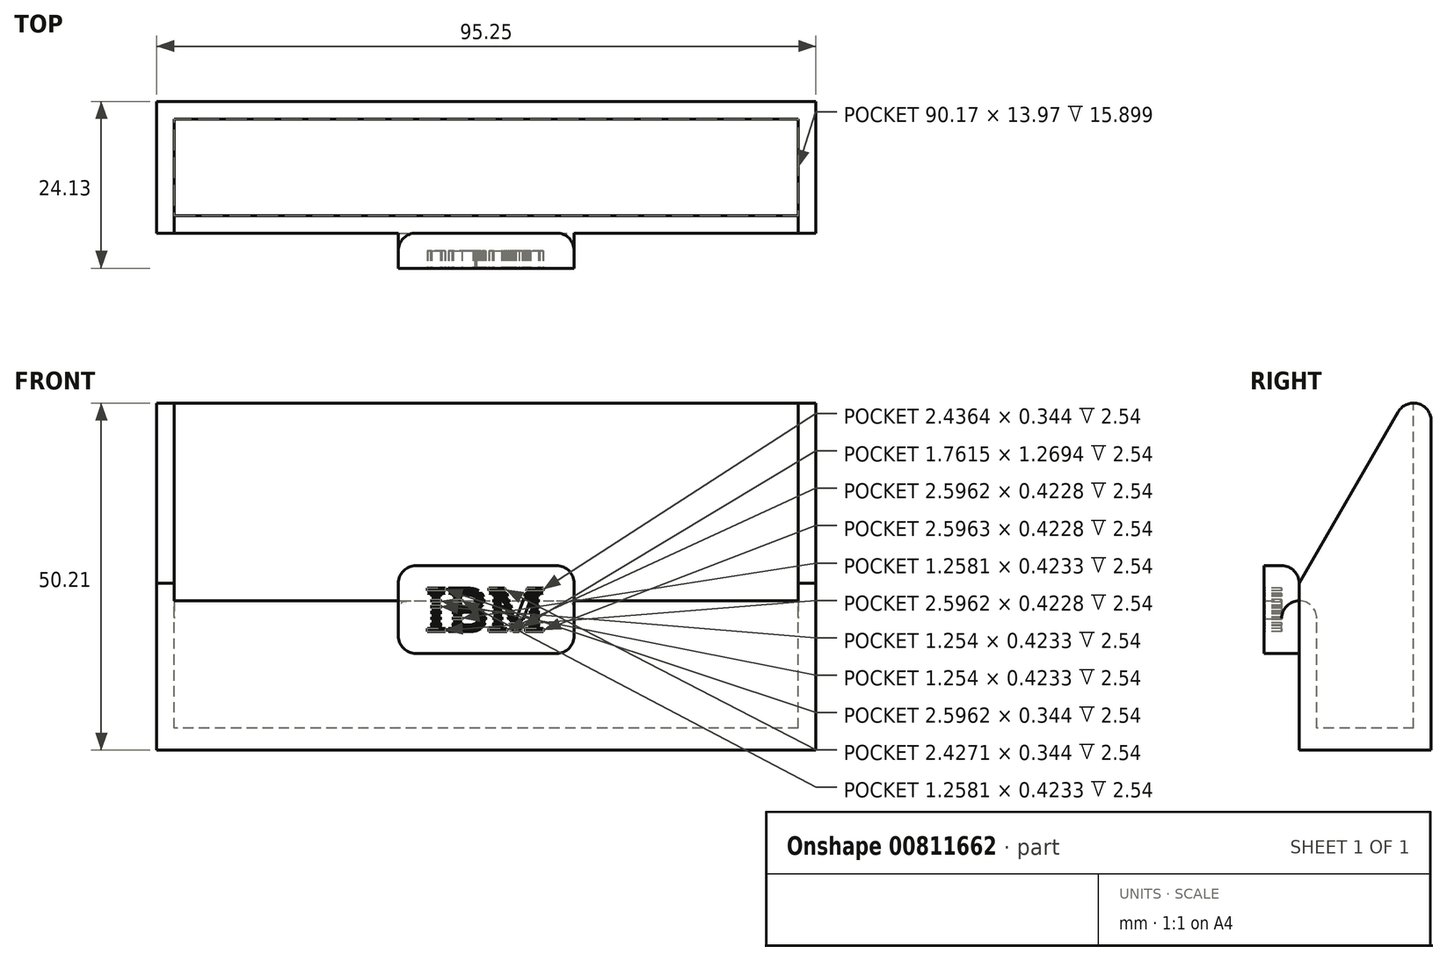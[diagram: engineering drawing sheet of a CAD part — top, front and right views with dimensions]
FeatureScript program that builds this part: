
annotation { "Feature Type Name" : "Feature", "Feature Type Description" : "" }
export const myFeature = defineFeature(function(context is Context, id is Id, definition is map)
    precondition{}
    {
        {
            var Q0;
            Q0=qCreatedBy(makeId("Top.planeOp"),FACE);
            var sketch = newSketch(context, id + "F0", { "sketchPlane" : qUnion([Q0])});
            skLineSegment(sketch, "E0.bottom", {"start": v(0, 0) * mm, "end": v(95.25, 0) * mm});
            skLineSegment(sketch, "E0.top", {"start": v(0, 19.05) * mm, "end": v(95.25, 19.05) * mm});
            skLineSegment(sketch, "E0.left", {"start": v(0, 0) * mm, "end": v(0, 19.05) * mm});
            skLineSegment(sketch, "E0.right", {"start": v(95.25, 0) * mm, "end": v(95.25, 19.05) * mm});
            skSolve(sketch);
        }
        {
            var Q0;
            Q0=makeQuery(id+"F0.imprint","IMPRINT",FACE,{"disambiguationData":[TD([[makeQuery(id+"F0.imprint","IMPRINT",EDGE,{"derivedFrom":sQuery(id+"F0.wireOp",EDGE,"E0.bottom")}),1.0]])]});
            extrude(context, id + "F1", {"entities" : qUnion([Q0]), "depth" : 57.15 * mm, "offsetDistance" : 25.4 * mm});
        }
        {
            var Q0;
            Q0=makeQuery(id+"F1.opExtrude","CAP_FACE",FACE,{"disambiguationData":[OSD([sQuery(id+"F0.wireOp",EDGE,"E0.bottom"),sQuery(id+"F0.wireOp",EDGE,"E0.top"),sQuery(id+"F0.wireOp",EDGE,"E0.left"),sQuery(id+"F0.wireOp",EDGE,"E0.right")])],"isStart":false});
            var sketch = newSketch(context, id + "F2", { "sketchPlane" : qUnion([Q0])});
            skLineSegment(sketch, "E1.bottom", {"start": v(92.71, 16.5) * mm, "end": v(2.54, 16.5) * mm});
            skLineSegment(sketch, "E1.top", {"start": v(92.71, 2.54) * mm, "end": v(2.54, 2.54) * mm});
            skLineSegment(sketch, "E1.left", {"start": v(92.71, 16.5) * mm, "end": v(92.71, 2.54) * mm});
            skLineSegment(sketch, "E1.right", {"start": v(2.54, 16.5) * mm, "end": v(2.54, 2.54) * mm});
            skPoint(sketch, "E1.middle", {"position": v(47.63, 9.52) * mm});
            skPoint(sketch, "E1.middle.positionSnap0", {"position": v(0, 9.52) * mm});
            skPoint(sketch, "E1.middle.positionSnap1", {"position": v(47.63, 19.05) * mm});
            skPoint(sketch, "E1.centerSnap0", {"position": v(0, 9.52) * mm});
            skPoint(sketch, "E1.centerSnap1", {"position": v(47.63, 19.05) * mm});
            skSolve(sketch);
        }
        {
            var Q0;
            Q0=makeQuery(id+"F2.imprint","IMPRINT",FACE,{"disambiguationData":[TD([[makeQuery(id+"F2.imprint","IMPRINT",EDGE,{"derivedFrom":sQuery(id+"F2.wireOp",EDGE,"E1.bottom")}),1.0]])]});
            extrude(context, id + "F3", {"entities" : qUnion([Q0]), "operationType" : NewBodyOperationType.REMOVE, "oppositeDirection" : true, "depth" : 53.97 * mm, "offsetDistance" : 25.4 * mm});
        }
        {
            var Q0;
            Q0=makeQuery(id+"F1.opExtrude","CAP_FACE",FACE,{"disambiguationData":[OSD([sQuery(id+"F0.wireOp",EDGE,"E0.bottom"),sQuery(id+"F0.wireOp",EDGE,"E0.top"),sQuery(id+"F0.wireOp",EDGE,"E0.left"),sQuery(id+"F0.wireOp",EDGE,"E0.right")])],"isStart":false});
            var Q1;
            Q1=makeQuery(id+"F1.opExtrude","CAP_EDGE",EDGE,{"disambiguationData":[OSD([sQuery(id+"F0.wireOp",EDGE,"E0.top")])],"isStart":false});
            cPlane(context, id + "F4", {"entities" : qUnion([Q0, Q1]), "cplaneType" : CPlaneType.LINE_ANGLE, "offset" : 25.4 * mm, "angle" : 60 * degree, "width" : 152.4 * mm, "height" : 152.4 * mm});
        }
        {
            var Q0;
            Q0=qCreatedBy(id+"F4.planeOp",FACE);
            var sketch = newSketch(context, id + "F5", { "sketchPlane" : qUnion([Q0])});
            skLineSegment(sketch, "E2.bottom", {"start": v(0, 59.02) * mm, "end": v(-95.25, 59.02) * mm});
            skLineSegment(sketch, "E2.top", {"start": v(0, 19.65) * mm, "end": v(-95.25, 19.65) * mm});
            skLineSegment(sketch, "E2.left", {"start": v(0, 59.02) * mm, "end": v(0, 19.65) * mm});
            skLineSegment(sketch, "E2.right", {"start": v(-95.25, 59.02) * mm, "end": v(-95.25, 19.65) * mm});
            skSolve(sketch);
        }
        {
            var Q0;
            Q0 = qSketchRegion(id + "F5", true);
            extrude(context, id + "F6", {"entities" : qUnion([Q0]), "operationType" : NewBodyOperationType.REMOVE, "oppositeDirection" : true, "depth" : 25.4 * mm, "offsetDistance" : 25.4 * mm});
        }
        {
            var Q0;
            Q0=makeQuery(id+"F6.boolean.opBoolean","MERGE",EDGE,{"derivedFrom":[makeQuery(id+"F1.opExtrude","CAP_EDGE",EDGE,{"disambiguationData":[OSD([sQuery(id+"F0.wireOp",EDGE,"E0.top")])],"isStart":false}),makeQuery(id+"F6.opExtrude","CAP_EDGE",EDGE,{"disambiguationData":[OSD([sQuery(id+"F5.wireOp",EDGE,"E2.bottom")])],"isStart":true})]});
            var Q1;
            Q1=makeQuery(id+"F6.boolean.opBoolean","INTERSECT",EDGE,{"derivedFrom":[makeQuery(id+"F3.boolean.opBoolean","COPY",FACE,{"derivedFrom":makeQuery(id+"F3.opExtrude","SWEPT_FACE",FACE,{"disambiguationData":[OSD([sQuery(id+"F2.wireOp",EDGE,"E1.top")])]})}),makeQuery(id+"F6.opExtrude","CAP_FACE",FACE,{"disambiguationData":[OSD([sQuery(id+"F5.wireOp",EDGE,"E2.bottom"),sQuery(id+"F5.wireOp",EDGE,"E2.top"),sQuery(id+"F5.wireOp",EDGE,"E2.left"),sQuery(id+"F5.wireOp",EDGE,"E2.right")])],"isStart":true})]});
            fillet(context, id + "F7", {"entities" : qUnion([Q0, Q1]), "radius" : 2.54 * mm, "tangentPropagation" : true, "allowEdgeOverflow" : false});
        }
        {
            var Q0;
            Q0=makeQuery(id+"F1.opExtrude","SWEPT_FACE",FACE,{"disambiguationData":[OSD([sQuery(id+"F0.wireOp",EDGE,"E0.bottom")])]});
            var sketch = newSketch(context, id + "F8", { "sketchPlane" : qUnion([Q0])});
            skLineSegment(sketch, "E3.bottom", {"start": v(57.79, 26.7) * mm, "end": v(37.47, 26.7) * mm});
            skLineSegment(sketch, "E3.top", {"start": v(57.79, 14) * mm, "end": v(37.47, 14) * mm});
            skLineSegment(sketch, "E3.left", {"start": v(60.33, 24.15) * mm, "end": v(60.33, 16.53) * mm});
            skLineSegment(sketch, "E3.right", {"start": v(34.93, 24.15) * mm, "end": v(34.93, 16.53) * mm});
            skPoint(sketch, "E3.middle", {"position": v(47.63, 20.34) * mm});
            skPoint(sketch, "E3.middle.positionSnap0", {"position": v(47.63, 21.61) * mm});
            skPoint(sketch, "E3.centerSnap0", {"position": v(47.63, 21.61) * mm});
            skPoint(sketch, "E4.visualSharp", {"position": v(34.93, 26.7) * mm});
            skArc(sketch, "E4.filletArc", {"start": v(37.47, 26.7) * mm, "mid": v(35.67, 25.95) * mm, "end": v(34.93, 24.15) * mm});
            skPoint(sketch, "E5.visualSharp", {"position": v(34.93, 14) * mm});
            skArc(sketch, "E5.filletArc", {"start": v(34.93, 16.53) * mm, "mid": v(35.67, 14.74) * mm, "end": v(37.47, 14) * mm});
            skPoint(sketch, "E6.visualSharp", {"position": v(60.33, 14) * mm});
            skArc(sketch, "E6.filletArc", {"start": v(57.79, 14) * mm, "mid": v(59.58, 14.74) * mm, "end": v(60.33, 16.53) * mm});
            skPoint(sketch, "E7.visualSharp", {"position": v(60.33, 26.7) * mm});
            skArc(sketch, "E7.filletArc", {"start": v(60.33, 24.15) * mm, "mid": v(59.58, 25.95) * mm, "end": v(57.79, 26.7) * mm});
            skSolve(sketch);
        }
        {
            var Q0;
            Q0 = qSketchRegion(id + "F8", true);
            extrude(context, id + "F9", {"entities" : qUnion([Q0]), "operationType" : NewBodyOperationType.ADD, "depth" : 5.08 * mm, "offsetDistance" : 25.4 * mm});
        }
        {
            var Q0;
            {var subQ0=sQuery(id+"F8.wireOp",EDGE,"E3.left");Q0=makeQuery(id+"F9.boolean.opBoolean","SPLIT",EDGE,{"disambiguationData":[topologyDisambiguationEdgeConnected([makeQuery(id+"F1.opExtrude","SWEPT_FACE",FACE,{"disambiguationData":[OSD([sQuery(id+"F0.wireOp",EDGE,"E0.bottom")])]})])],"derivedFrom":makeQuery(id+"F9.opExtrude","CAP_EDGE",EDGE,{"disambiguationData":[OSD([subQ0])],"isStart":true})});}
            var Q1;
            Q1=makeQuery(id+"F9.opExtrude","CAP_EDGE",EDGE,{"disambiguationData":[OSD([sQuery(id+"F8.wireOp",EDGE,"E6.filletArc")])],"isStart":true});
            var Q2;
            Q2=makeQuery(id+"F9.opExtrude","CAP_EDGE",EDGE,{"disambiguationData":[OSD([sQuery(id+"F8.wireOp",EDGE,"E3.top")])],"isStart":true});
            var Q3;
            Q3=makeQuery(id+"F9.opExtrude","CAP_EDGE",EDGE,{"disambiguationData":[OSD([sQuery(id+"F8.wireOp",EDGE,"E5.filletArc")])],"isStart":true});
            var Q4;
            {var subQ0=sQuery(id+"F8.wireOp",EDGE,"E3.right");Q4=makeQuery(id+"F9.boolean.opBoolean","SPLIT",EDGE,{"disambiguationData":[topologyDisambiguationEdgeConnected([makeQuery(id+"F1.opExtrude","SWEPT_FACE",FACE,{"disambiguationData":[OSD([sQuery(id+"F0.wireOp",EDGE,"E0.bottom")])]})])],"derivedFrom":makeQuery(id+"F9.opExtrude","CAP_EDGE",EDGE,{"disambiguationData":[OSD([subQ0])],"isStart":true})});}
            fillet(context, id + "F10", {"entities" : qUnion([Q0, Q1, Q2, Q3, Q4]), "radius" : 2.54 * mm, "tangentPropagation" : true, "allowEdgeOverflow" : false});
        }
        {
            var Q0;
            Q0=makeQuery(id+"F9.opExtrude","CAP_FACE",FACE,{"disambiguationData":[OSD([sQuery(id+"F8.wireOp",EDGE,"E3.bottom"),sQuery(id+"F8.wireOp",EDGE,"E3.top"),sQuery(id+"F8.wireOp",EDGE,"E3.left"),sQuery(id+"F8.wireOp",EDGE,"E3.right"),sQuery(id+"F8.wireOp",EDGE,"E4.filletArc"),sQuery(id+"F8.wireOp",EDGE,"E5.filletArc"),sQuery(id+"F8.wireOp",EDGE,"E6.filletArc"),sQuery(id+"F8.wireOp",EDGE,"E7.filletArc")])],"isStart":false});
            var sketch = newSketch(context, id + "F11", { "sketchPlane" : qUnion([Q0])});
            skText(sketch, "E8", { "text": "IBM", "fontName": "RobotoSlab-Bold.ttf"});
            skLineSegment(sketch, "E9", {"start": v(47.63, 23.52) * mm, "end": v(47.63, 26.7) * mm, "construction": true});
            skLineSegment(sketch, "E10", {"start": v(47.63, 17.17) * mm, "end": v(47.63, 14) * mm, "construction": true});
            skLineSegment(sketch, "E11.bottom", {"start": v(38.85, 23.52) * mm, "end": v(56.4, 23.52) * mm});
            skLineSegment(sketch, "E11.top", {"start": v(38.85, 23.1) * mm, "end": v(56.4, 23.1) * mm});
            skLineSegment(sketch, "E11.left", {"start": v(38.85, 23.52) * mm, "end": v(38.85, 23.1) * mm});
            skLineSegment(sketch, "E11.right", {"start": v(56.4, 23.52) * mm, "end": v(56.4, 23.1) * mm});
            skLineSegment(sketch, "E12.0.1.0", {"start": v(38.85, 22.67) * mm, "end": v(56.4, 22.67) * mm});
            skLineSegment(sketch, "E12.0.2.0", {"start": v(38.85, 22.25) * mm, "end": v(56.4, 22.25) * mm});
            skLineSegment(sketch, "E12.0.3.0", {"start": v(38.85, 21.83) * mm, "end": v(56.4, 21.83) * mm});
            skLineSegment(sketch, "E12.0.4.0", {"start": v(38.85, 21.4) * mm, "end": v(56.4, 21.4) * mm});
            skLineSegment(sketch, "E12.0.5.0", {"start": v(38.85, 20.98) * mm, "end": v(56.4, 20.98) * mm});
            skLineSegment(sketch, "E12.0.6.0", {"start": v(38.85, 20.56) * mm, "end": v(56.4, 20.56) * mm});
            skLineSegment(sketch, "E12.0.7.0", {"start": v(38.85, 20.13) * mm, "end": v(56.4, 20.13) * mm});
            skLineSegment(sketch, "E12.0.8.0", {"start": v(38.85, 19.7) * mm, "end": v(56.4, 19.7) * mm});
            skLineSegment(sketch, "E12.0.9.0", {"start": v(38.85, 19.29) * mm, "end": v(56.4, 19.29) * mm});
            skLineSegment(sketch, "E12.0.10.0", {"start": v(38.85, 18.86) * mm, "end": v(56.4, 18.86) * mm});
            skLineSegment(sketch, "E12.0.11.0", {"start": v(38.85, 18.44) * mm, "end": v(56.4, 18.44) * mm});
            skLineSegment(sketch, "E12.0.12.0", {"start": v(38.85, 18.02) * mm, "end": v(56.4, 18.02) * mm});
            skLineSegment(sketch, "E12.0.13.0", {"start": v(38.85, 17.6) * mm, "end": v(56.4, 17.6) * mm});
            skLineSegment(sketch, "E12.0.14.0", {"start": v(38.85, 17.17) * mm, "end": v(56.4, 17.17) * mm});
            skLineSegment(sketch, "E12.direction1", {"start": v(38.85, 23.1) * mm, "end": v(64.25, 23.1) * mm, "construction": true});
            skLineSegment(sketch, "E12.direction2", {"start": v(38.85, 23.1) * mm, "end": v(38.85, 22.67) * mm, "construction": true});
            const initialGuessF11  = {"E8": [0.03885, 0.01717, 1, 0, 0.00635]};
            skSetInitialGuess(sketch, initialGuessF11);
            skSolve(sketch);
        }
        {
            var Q0;
            {var subQ0=sQuery(id+"F11.wireOp",EDGE,"E8.sketch_text.stroke-62");Q0=makeQuery(id+"F11.imprint","IMPRINT",FACE,{"disambiguationData":[TD([[makeQuery(id+"F11.imprint","IMPRINT",EDGE,{"derivedFrom":subQ0}),-1.0]])]});}
            var Q1;
            {var subQ6=sQuery(id+"F11.wireOp",EDGE,"E8.sketch_text.stroke-57");Q1=makeQuery(id+"F11.imprint","IMPRINT",FACE,{"disambiguationData":[TD([[makeQuery(id+"F11.imprint","IMPRINT",EDGE,{"derivedFrom":subQ6}),-1.0]])]});}
            var Q2;
            {var subQ1=sQuery(id+"F11.wireOp",EDGE,"E8.sketch_text.stroke-26");Q2=makeQuery(id+"F11.imprint","IMPRINT",FACE,{"disambiguationData":[TD([[makeQuery(id+"F11.imprint","IMPRINT",EDGE,{"derivedFrom":subQ1}),-1.0]])]});}
            var Q3;
            {var subQ0=sQuery(id+"F11.wireOp",EDGE,"E8.sketch_text.stroke-1");Q3=makeQuery(id+"F11.imprint","IMPRINT",FACE,{"disambiguationData":[TD([[makeQuery(id+"F11.imprint","IMPRINT",EDGE,{"derivedFrom":subQ0}),-1.0]])]});}
            var Q4;
            {var subQ5=sQuery(id+"F11.wireOp",EDGE,"E8.sketch_text.stroke-4");var subQ6=sQuery(id+"F11.wireOp",EDGE,"E8.sketch_text.stroke-3");var subQ7=makeQuery(id+"F11.imprint","INTERSECT",VERTEX,{"derivedFrom":[subQ6,subQ5]});Q4=makeQuery(id+"F11.imprint","IMPRINT",FACE,{"disambiguationData":[TD([[makeQuery(id+"F11.imprint","IMPRINT",EDGE,{"disambiguationData":[TD([[subQ7,1.0]])],"derivedFrom":subQ6}),-1.0]])]});}
            var Q5;
            {var subQ0=sQuery(id+"F11.wireOp",EDGE,"E12.0.3.0");var subQ1=sQuery(id+"F11.wireOp",EDGE,"E8.sketch_text.stroke-4");var subQ2=makeQuery(id+"F11.imprint","INTERSECT",VERTEX,{"derivedFrom":[subQ1,subQ0]});Q5=makeQuery(id+"F11.imprint","IMPRINT",FACE,{"disambiguationData":[TD([[makeQuery(id+"F11.imprint","IMPRINT",EDGE,{"disambiguationData":[TD([[subQ2,-1.0]])],"derivedFrom":subQ1}),-1.0]])]});}
            var Q6;
            {var subQ0=sQuery(id+"F11.wireOp",EDGE,"E12.0.5.0");var subQ1=sQuery(id+"F11.wireOp",EDGE,"E8.sketch_text.stroke-4");var subQ2=makeQuery(id+"F11.imprint","INTERSECT",VERTEX,{"derivedFrom":[subQ1,subQ0]});Q6=makeQuery(id+"F11.imprint","IMPRINT",FACE,{"disambiguationData":[TD([[makeQuery(id+"F11.imprint","IMPRINT",EDGE,{"disambiguationData":[TD([[subQ2,-1.0]])],"derivedFrom":subQ1}),-1.0]])]});}
            var Q7;
            {var subQ0=sQuery(id+"F11.wireOp",EDGE,"E12.0.7.0");var subQ1=sQuery(id+"F11.wireOp",EDGE,"E8.sketch_text.stroke-4");var subQ2=makeQuery(id+"F11.imprint","INTERSECT",VERTEX,{"derivedFrom":[subQ1,subQ0]});Q7=makeQuery(id+"F11.imprint","IMPRINT",FACE,{"disambiguationData":[TD([[makeQuery(id+"F11.imprint","IMPRINT",EDGE,{"disambiguationData":[TD([[subQ2,-1.0]])],"derivedFrom":subQ1}),-1.0]])]});}
            var Q8;
            {var subQ0=sQuery(id+"F11.wireOp",EDGE,"E12.0.9.0");var subQ1=sQuery(id+"F11.wireOp",EDGE,"E8.sketch_text.stroke-4");var subQ2=makeQuery(id+"F11.imprint","INTERSECT",VERTEX,{"derivedFrom":[subQ1,subQ0]});Q8=makeQuery(id+"F11.imprint","IMPRINT",FACE,{"disambiguationData":[TD([[makeQuery(id+"F11.imprint","IMPRINT",EDGE,{"disambiguationData":[TD([[subQ2,-1.0]])],"derivedFrom":subQ1}),-1.0]])]});}
            var Q9;
            {var subQ7=sQuery(id+"F11.wireOp",EDGE,"E8.sketch_text.stroke-5");var subQ8=sQuery(id+"F11.wireOp",EDGE,"E8.sketch_text.stroke-4");var subQ9=makeQuery(id+"F11.imprint","INTERSECT",VERTEX,{"derivedFrom":[subQ8,subQ7]});Q9=makeQuery(id+"F11.imprint","IMPRINT",FACE,{"disambiguationData":[TD([[makeQuery(id+"F11.imprint","IMPRINT",EDGE,{"disambiguationData":[TD([[subQ9,1.0]])],"derivedFrom":subQ8}),-1.0]])]});}
            var Q10;
            {var subQ0=sQuery(id+"F11.wireOp",EDGE,"E12.0.14.0");var subQ1=sQuery(id+"F11.wireOp",EDGE,"E8.sketch_text.stroke-6");var subQ2=makeQuery(id+"F11.imprint","INTERSECT",VERTEX,{"derivedFrom":[subQ1,subQ0]});Q10=makeQuery(id+"F11.imprint","IMPRINT",FACE,{"disambiguationData":[TD([[makeQuery(id+"F11.imprint","IMPRINT",EDGE,{"disambiguationData":[TD([[subQ2,1.0]])],"derivedFrom":subQ1}),-1.0]])]});}
            var Q11;
            {var subQ0=sQuery(id+"F11.wireOp",EDGE,"E12.0.14.0");var subQ1=sQuery(id+"F11.wireOp",EDGE,"E8.sketch_text.stroke-19");var subQ2=makeQuery(id+"F11.imprint","INTERSECT",VERTEX,{"derivedFrom":[subQ1,subQ0]});Q11=makeQuery(id+"F11.imprint","IMPRINT",FACE,{"disambiguationData":[TD([[makeQuery(id+"F11.imprint","IMPRINT",EDGE,{"disambiguationData":[TD([[subQ2,1.0]])],"derivedFrom":subQ1}),-1.0]])]});}
            var Q12;
            {var subQ0=sQuery(id+"F11.wireOp",EDGE,"E8.sketch_text.stroke-29");Q12=makeQuery(id+"F11.imprint","IMPRINT",FACE,{"disambiguationData":[TD([[makeQuery(id+"F11.imprint","IMPRINT",EDGE,{"derivedFrom":subQ0}),-1.0]])]});}
            var Q13;
            {var subQ0=sQuery(id+"F11.wireOp",EDGE,"E12.0.10.0");var subQ1=sQuery(id+"F11.wireOp",EDGE,"E8.sketch_text.stroke-23");var subQ2=makeQuery(id+"F11.imprint","INTERSECT",VERTEX,{"derivedFrom":[subQ1,subQ0]});Q13=makeQuery(id+"F11.imprint","IMPRINT",FACE,{"disambiguationData":[TD([[makeQuery(id+"F11.imprint","IMPRINT",EDGE,{"disambiguationData":[TD([[subQ2,-1.0]])],"derivedFrom":subQ1}),-1.0]])]});}
            var Q14;
            {var subQ6=sQuery(id+"F11.wireOp",EDGE,"E8.sketch_text.stroke-18");var subQ9=sQuery(id+"F11.wireOp",EDGE,"E8.sketch_text.stroke-17");var subQ10=makeQuery(id+"F11.imprint","INTERSECT",VERTEX,{"derivedFrom":[subQ9,subQ6]});Q14=makeQuery(id+"F11.imprint","IMPRINT",FACE,{"disambiguationData":[TD([[makeQuery(id+"F11.imprint","IMPRINT",EDGE,{"disambiguationData":[TD([[subQ10,1.0]])],"derivedFrom":subQ9}),-1.0]])]});}
            var Q15;
            {var subQ5=sQuery(id+"F11.wireOp",EDGE,"E8.sketch_text.stroke-34");Q15=makeQuery(id+"F11.imprint","IMPRINT",FACE,{"disambiguationData":[TD([[makeQuery(id+"F11.imprint","IMPRINT",EDGE,{"derivedFrom":subQ5}),-1.0]])]});}
            var Q16;
            {var subQ9=sQuery(id+"F11.wireOp",EDGE,"E8.sketch_text.stroke-35");Q16=makeQuery(id+"F11.imprint","IMPRINT",FACE,{"disambiguationData":[TD([[makeQuery(id+"F11.imprint","IMPRINT",EDGE,{"derivedFrom":subQ9}),-1.0]])]});}
            var Q17;
            {var subQ7=sQuery(id+"F11.wireOp",EDGE,"E8.sketch_text.stroke-14");var subQ8=sQuery(id+"F11.wireOp",EDGE,"E8.sketch_text.stroke-13");var subQ9=makeQuery(id+"F11.imprint","INTERSECT",VERTEX,{"derivedFrom":[subQ8,subQ7]});Q17=makeQuery(id+"F11.imprint","IMPRINT",FACE,{"disambiguationData":[TD([[makeQuery(id+"F11.imprint","IMPRINT",EDGE,{"disambiguationData":[TD([[subQ9,1.0]])],"derivedFrom":subQ8}),-1.0]])]});}
            var Q18;
            {var subQ0=sQuery(id+"F11.wireOp",EDGE,"E12.0.4.0");var subQ1=sQuery(id+"F11.wireOp",EDGE,"E8.sketch_text.stroke-23");var subQ2=makeQuery(id+"F11.imprint","INTERSECT",VERTEX,{"derivedFrom":[subQ1,subQ0]});Q18=makeQuery(id+"F11.imprint","IMPRINT",FACE,{"disambiguationData":[TD([[makeQuery(id+"F11.imprint","IMPRINT",EDGE,{"disambiguationData":[TD([[subQ2,-1.0]])],"derivedFrom":subQ1}),-1.0]])]});}
            var Q19;
            {var subQ0=sQuery(id+"F11.wireOp",EDGE,"E8.sketch_text.stroke-39");Q19=makeQuery(id+"F11.imprint","IMPRINT",FACE,{"disambiguationData":[TD([[makeQuery(id+"F11.imprint","IMPRINT",EDGE,{"derivedFrom":subQ0}),-1.0]])]});}
            var Q20;
            {var subQ1=sQuery(id+"F11.wireOp",EDGE,"E8.sketch_text.stroke-55");var subQ7=sQuery(id+"F11.wireOp",EDGE,"E8.sketch_text.stroke-54");var subQ8=makeQuery(id+"F11.imprint","INTERSECT",VERTEX,{"derivedFrom":[subQ7,subQ1]});Q20=makeQuery(id+"F11.imprint","IMPRINT",FACE,{"disambiguationData":[TD([[makeQuery(id+"F11.imprint","IMPRINT",EDGE,{"disambiguationData":[TD([[subQ8,1.0]])],"derivedFrom":subQ7}),-1.0]])]});}
            var Q21;
            {var subQ3=sQuery(id+"F11.wireOp",EDGE,"E12.0.2.0");var subQ7=sQuery(id+"F11.wireOp",EDGE,"E8.sketch_text.stroke-61");var subQ9=makeQuery(id+"F11.imprint","INTERSECT",VERTEX,{"derivedFrom":[subQ7,subQ3]});Q21=makeQuery(id+"F11.imprint","IMPRINT",FACE,{"disambiguationData":[TD([[makeQuery(id+"F11.imprint","IMPRINT",EDGE,{"disambiguationData":[TD([[subQ9,-1.0]])],"derivedFrom":subQ7}),-1.0]])]});}
            var Q22;
            {var subQ11=sQuery(id+"F11.wireOp",EDGE,"E8.sketch_text.stroke-42");Q22=makeQuery(id+"F11.imprint","IMPRINT",FACE,{"disambiguationData":[TD([[makeQuery(id+"F11.imprint","IMPRINT",EDGE,{"derivedFrom":subQ11}),-1.0]])]});}
            var Q23;
            {var subQ6=sQuery(id+"F11.wireOp",EDGE,"E8.sketch_text.stroke-46");Q23=makeQuery(id+"F11.imprint","IMPRINT",FACE,{"disambiguationData":[TD([[makeQuery(id+"F11.imprint","IMPRINT",EDGE,{"derivedFrom":subQ6}),-1.0]])]});}
            var Q24;
            {var subQ0=sQuery(id+"F11.wireOp",EDGE,"E12.0.6.0");var subQ1=sQuery(id+"F11.wireOp",EDGE,"E8.sketch_text.stroke-45");var subQ2=makeQuery(id+"F11.imprint","INTERSECT",VERTEX,{"derivedFrom":[subQ1,subQ0]});Q24=makeQuery(id+"F11.imprint","IMPRINT",FACE,{"disambiguationData":[TD([[makeQuery(id+"F11.imprint","IMPRINT",EDGE,{"disambiguationData":[TD([[subQ2,-1.0]])],"derivedFrom":subQ1}),-1.0]])]});}
            var Q25;
            {var subQ0=sQuery(id+"F11.wireOp",EDGE,"E12.0.5.0");var subQ1=sQuery(id+"F11.wireOp",EDGE,"E8.sketch_text.stroke-47");var subQ2=makeQuery(id+"F11.imprint","INTERSECT",VERTEX,{"derivedFrom":[subQ1,subQ0]});Q25=makeQuery(id+"F11.imprint","IMPRINT",FACE,{"disambiguationData":[TD([[makeQuery(id+"F11.imprint","IMPRINT",EDGE,{"disambiguationData":[TD([[subQ2,-1.0]])],"derivedFrom":subQ1}),-1.0]])]});}
            var Q26;
            {var subQ0=sQuery(id+"F11.wireOp",EDGE,"E12.0.5.0");var subQ1=sQuery(id+"F11.wireOp",EDGE,"E8.sketch_text.stroke-43");var subQ2=makeQuery(id+"F11.imprint","INTERSECT",VERTEX,{"derivedFrom":[subQ1,subQ0]});Q26=makeQuery(id+"F11.imprint","IMPRINT",FACE,{"disambiguationData":[TD([[makeQuery(id+"F11.imprint","IMPRINT",EDGE,{"disambiguationData":[TD([[subQ2,-1.0]])],"derivedFrom":subQ1}),-1.0]])]});}
            var Q27;
            {var subQ0=sQuery(id+"F11.wireOp",EDGE,"E12.0.5.0");var subQ1=sQuery(id+"F11.wireOp",EDGE,"E8.sketch_text.stroke-65");var subQ2=makeQuery(id+"F11.imprint","INTERSECT",VERTEX,{"derivedFrom":[subQ1,subQ0]});Q27=makeQuery(id+"F11.imprint","IMPRINT",FACE,{"disambiguationData":[TD([[makeQuery(id+"F11.imprint","IMPRINT",EDGE,{"disambiguationData":[TD([[subQ2,-1.0]])],"derivedFrom":subQ1}),-1.0]])]});}
            var Q28;
            {var subQ0=sQuery(id+"F11.wireOp",EDGE,"E12.0.7.0");var subQ1=sQuery(id+"F11.wireOp",EDGE,"E8.sketch_text.stroke-65");var subQ2=makeQuery(id+"F11.imprint","INTERSECT",VERTEX,{"derivedFrom":[subQ1,subQ0]});Q28=makeQuery(id+"F11.imprint","IMPRINT",FACE,{"disambiguationData":[TD([[makeQuery(id+"F11.imprint","IMPRINT",EDGE,{"disambiguationData":[TD([[subQ2,-1.0]])],"derivedFrom":subQ1}),-1.0]])]});}
            var Q29;
            {var subQ0=sQuery(id+"F11.wireOp",EDGE,"E12.0.7.0");var subQ1=sQuery(id+"F11.wireOp",EDGE,"E8.sketch_text.stroke-43");var subQ2=makeQuery(id+"F11.imprint","INTERSECT",VERTEX,{"derivedFrom":[subQ1,subQ0]});Q29=makeQuery(id+"F11.imprint","IMPRINT",FACE,{"disambiguationData":[TD([[makeQuery(id+"F11.imprint","IMPRINT",EDGE,{"disambiguationData":[TD([[subQ2,-1.0]])],"derivedFrom":subQ1}),-1.0]])]});}
            var Q30;
            {var subQ0=sQuery(id+"F11.wireOp",EDGE,"E12.0.8.0");var subQ1=sQuery(id+"F11.wireOp",EDGE,"E8.sketch_text.stroke-45");var subQ2=makeQuery(id+"F11.imprint","INTERSECT",VERTEX,{"derivedFrom":[subQ1,subQ0]});Q30=makeQuery(id+"F11.imprint","IMPRINT",FACE,{"disambiguationData":[TD([[makeQuery(id+"F11.imprint","IMPRINT",EDGE,{"disambiguationData":[TD([[subQ2,-1.0]])],"derivedFrom":subQ1}),-1.0]])]});}
            var Q31;
            {var subQ0=sQuery(id+"F11.wireOp",EDGE,"E12.0.7.0");var subQ1=sQuery(id+"F11.wireOp",EDGE,"E8.sketch_text.stroke-47");var subQ2=makeQuery(id+"F11.imprint","INTERSECT",VERTEX,{"derivedFrom":[subQ1,subQ0]});Q31=makeQuery(id+"F11.imprint","IMPRINT",FACE,{"disambiguationData":[TD([[makeQuery(id+"F11.imprint","IMPRINT",EDGE,{"disambiguationData":[TD([[subQ2,-1.0]])],"derivedFrom":subQ1}),-1.0]])]});}
            var Q32;
            {var subQ1=sQuery(id+"F11.wireOp",EDGE,"E8.sketch_text.stroke-47");var subQ7=sQuery(id+"F11.wireOp",EDGE,"E8.sketch_text.stroke-48");var subQ8=makeQuery(id+"F11.imprint","INTERSECT",VERTEX,{"derivedFrom":[subQ1,subQ7]});Q32=makeQuery(id+"F11.imprint","IMPRINT",FACE,{"disambiguationData":[TD([[makeQuery(id+"F11.imprint","IMPRINT",EDGE,{"disambiguationData":[TD([[subQ8,1.0]])],"derivedFrom":subQ1}),-1.0]])]});}
            var Q33;
            {var subQ0=sQuery(id+"F11.wireOp",EDGE,"E12.0.10.0");var subQ1=sQuery(id+"F11.wireOp",EDGE,"E8.sketch_text.stroke-45");var subQ2=makeQuery(id+"F11.imprint","INTERSECT",VERTEX,{"derivedFrom":[subQ1,subQ0]});Q33=makeQuery(id+"F11.imprint","IMPRINT",FACE,{"disambiguationData":[TD([[makeQuery(id+"F11.imprint","IMPRINT",EDGE,{"disambiguationData":[TD([[subQ2,-1.0]])],"derivedFrom":subQ1}),-1.0]])]});}
            var Q34;
            {var subQ0=sQuery(id+"F11.wireOp",EDGE,"E12.0.9.0");var subQ1=sQuery(id+"F11.wireOp",EDGE,"E8.sketch_text.stroke-43");var subQ2=makeQuery(id+"F11.imprint","INTERSECT",VERTEX,{"derivedFrom":[subQ1,subQ0]});Q34=makeQuery(id+"F11.imprint","IMPRINT",FACE,{"disambiguationData":[TD([[makeQuery(id+"F11.imprint","IMPRINT",EDGE,{"disambiguationData":[TD([[subQ2,-1.0]])],"derivedFrom":subQ1}),-1.0]])]});}
            var Q35;
            {var subQ0=sQuery(id+"F11.wireOp",EDGE,"E12.0.9.0");var subQ1=sQuery(id+"F11.wireOp",EDGE,"E8.sketch_text.stroke-65");var subQ2=makeQuery(id+"F11.imprint","INTERSECT",VERTEX,{"derivedFrom":[subQ1,subQ0]});Q35=makeQuery(id+"F11.imprint","IMPRINT",FACE,{"disambiguationData":[TD([[makeQuery(id+"F11.imprint","IMPRINT",EDGE,{"disambiguationData":[TD([[subQ2,-1.0]])],"derivedFrom":subQ1}),-1.0]])]});}
            var Q36;
            {var subQ7=sQuery(id+"F11.wireOp",EDGE,"E8.sketch_text.stroke-66");var subQ9=sQuery(id+"F11.wireOp",EDGE,"E8.sketch_text.stroke-65");var subQ10=makeQuery(id+"F11.imprint","INTERSECT",VERTEX,{"derivedFrom":[subQ9,subQ7]});Q36=makeQuery(id+"F11.imprint","IMPRINT",FACE,{"disambiguationData":[TD([[makeQuery(id+"F11.imprint","IMPRINT",EDGE,{"disambiguationData":[TD([[subQ10,1.0]])],"derivedFrom":subQ9}),-1.0]])]});}
            var Q37;
            {var subQ0=sQuery(id+"F11.wireOp",EDGE,"E12.0.11.0");var subQ1=sQuery(id+"F11.wireOp",EDGE,"E8.sketch_text.stroke-43");var subQ2=makeQuery(id+"F11.imprint","INTERSECT",VERTEX,{"derivedFrom":[subQ1,subQ0]});Q37=makeQuery(id+"F11.imprint","IMPRINT",FACE,{"disambiguationData":[TD([[makeQuery(id+"F11.imprint","IMPRINT",EDGE,{"disambiguationData":[TD([[subQ2,-1.0]])],"derivedFrom":subQ1}),-1.0]])]});}
            var Q38;
            {var subQ7=sQuery(id+"F11.wireOp",EDGE,"E8.sketch_text.stroke-49");var subQ8=sQuery(id+"F11.wireOp",EDGE,"E8.sketch_text.stroke-48");var subQ9=makeQuery(id+"F11.imprint","INTERSECT",VERTEX,{"derivedFrom":[subQ8,subQ7]});Q38=makeQuery(id+"F11.imprint","IMPRINT",FACE,{"disambiguationData":[TD([[makeQuery(id+"F11.imprint","IMPRINT",EDGE,{"disambiguationData":[TD([[subQ9,1.0]])],"derivedFrom":subQ8}),-1.0]])]});}
            var Q39;
            {var subQ0=sQuery(id+"F11.wireOp",EDGE,"E12.0.14.0");var subQ1=sQuery(id+"F11.wireOp",EDGE,"E8.sketch_text.stroke-50");var subQ2=makeQuery(id+"F11.imprint","INTERSECT",VERTEX,{"derivedFrom":[subQ1,subQ0]});Q39=makeQuery(id+"F11.imprint","IMPRINT",FACE,{"disambiguationData":[TD([[makeQuery(id+"F11.imprint","IMPRINT",EDGE,{"disambiguationData":[TD([[subQ2,1.0]])],"derivedFrom":subQ1}),-1.0]])]});}
            var Q40;
            {var subQ0=sQuery(id+"F11.wireOp",EDGE,"E12.0.14.0");var subQ1=sQuery(id+"F11.wireOp",EDGE,"E8.sketch_text.stroke-43");var subQ2=makeQuery(id+"F11.imprint","INTERSECT",VERTEX,{"derivedFrom":[subQ1,subQ0]});Q40=makeQuery(id+"F11.imprint","IMPRINT",FACE,{"disambiguationData":[TD([[makeQuery(id+"F11.imprint","IMPRINT",EDGE,{"disambiguationData":[TD([[subQ2,1.0]])],"derivedFrom":subQ1}),-1.0]])]});}
            var Q41;
            {var subQ0=sQuery(id+"F11.wireOp",EDGE,"E12.0.14.0");var subQ1=sQuery(id+"F11.wireOp",EDGE,"E8.sketch_text.stroke-67");var subQ2=makeQuery(id+"F11.imprint","INTERSECT",VERTEX,{"derivedFrom":[subQ1,subQ0]});Q41=makeQuery(id+"F11.imprint","IMPRINT",FACE,{"disambiguationData":[TD([[makeQuery(id+"F11.imprint","IMPRINT",EDGE,{"disambiguationData":[TD([[subQ2,1.0]])],"derivedFrom":subQ1}),-1.0]])]});}
            extrude(context, id + "F12", {"entities" : qUnion([Q0, Q1, Q2, Q3, Q4, Q5, Q6, Q7, Q8, Q9, Q10, Q11, Q12, Q13, Q14, Q15, Q16, Q17, Q18, Q19, Q20, Q21, Q22, Q23, Q24, Q25, Q26, Q27, Q28, Q29, Q30, Q31, Q32, Q33, Q34, Q35, Q36, Q37, Q38, Q39, Q40, Q41]), "operationType" : NewBodyOperationType.REMOVE, "oppositeDirection" : true, "depth" : 2.54 * mm, "offsetDistance" : 25.4 * mm});
        }
    });
